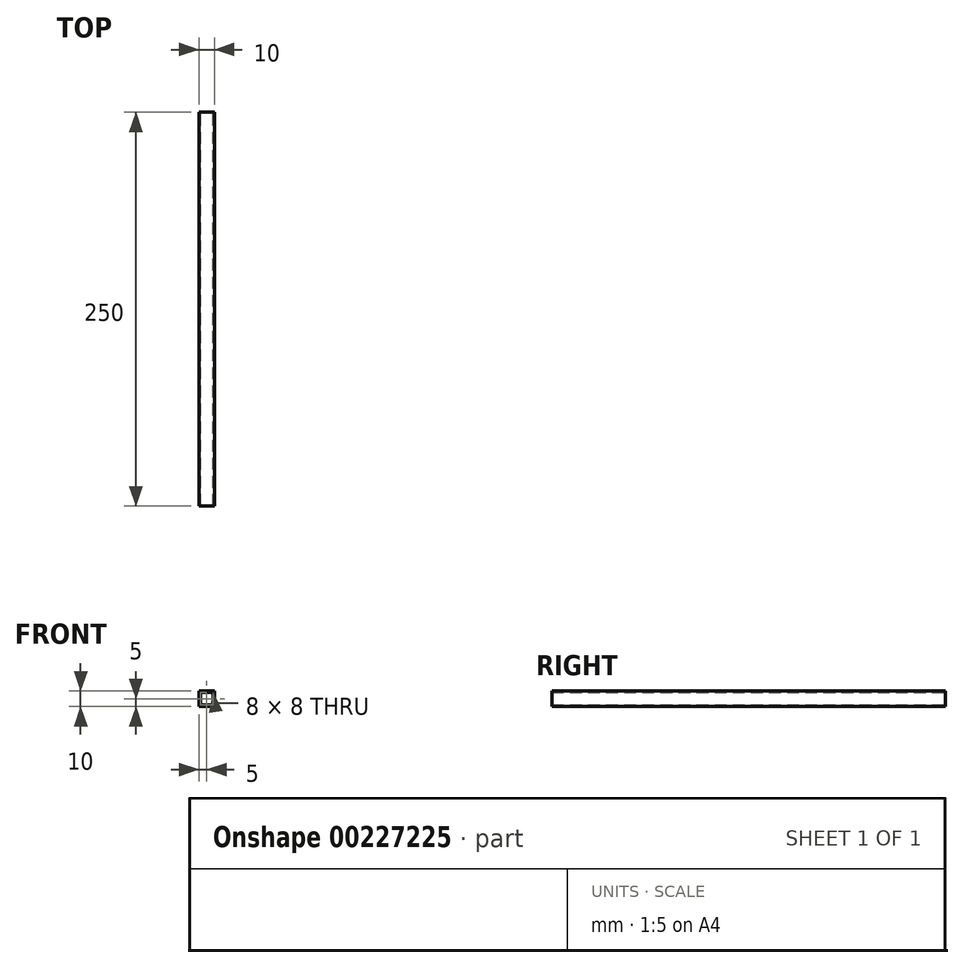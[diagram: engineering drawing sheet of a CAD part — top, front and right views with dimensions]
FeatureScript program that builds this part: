
annotation { "Feature Type Name" : "Feature", "Feature Type Description" : "" }
export const myFeature = defineFeature(function(context is Context, id is Id, definition is map)
    precondition{}
    {
        {
            var Q0;
            Q0=qCreatedBy(makeId("Front.planeOp"),FACE);
            var sketch = newSketch(context, id + "F0", { "sketchPlane" : qUnion([Q0])});
            skLineSegment(sketch, "E0.bottom", {"start": v(5, -5) * mm, "end": v(-5, -5) * mm});
            skLineSegment(sketch, "E0.top", {"start": v(5, 5) * mm, "end": v(-5, 5) * mm});
            skLineSegment(sketch, "E0.left", {"start": v(5, -5) * mm, "end": v(5, 5) * mm});
            skLineSegment(sketch, "E0.right", {"start": v(-5, -5) * mm, "end": v(-5, 5) * mm});
            skPoint(sketch, "E0.middle", {"position": v(0, 0) * mm});
            skLineSegment(sketch, "E1.bottom", {"start": v(4, -4) * mm, "end": v(-4, -4) * mm});
            skLineSegment(sketch, "E1.top", {"start": v(4, 4) * mm, "end": v(-4, 4) * mm});
            skLineSegment(sketch, "E1.left", {"start": v(4, -4) * mm, "end": v(4, 4) * mm});
            skLineSegment(sketch, "E1.right", {"start": v(-4, -4) * mm, "end": v(-4, 4) * mm});
            skSolve(sketch);
        }
        {
            var Q0;
            Q0 = qSketchRegion(id + "F0", true);
            extrude(context, id + "F1", {"entities" : qUnion([Q0]), "endBound" : BoundingType.SYMMETRIC, "depth" : 250 * mm});
        }
    });
